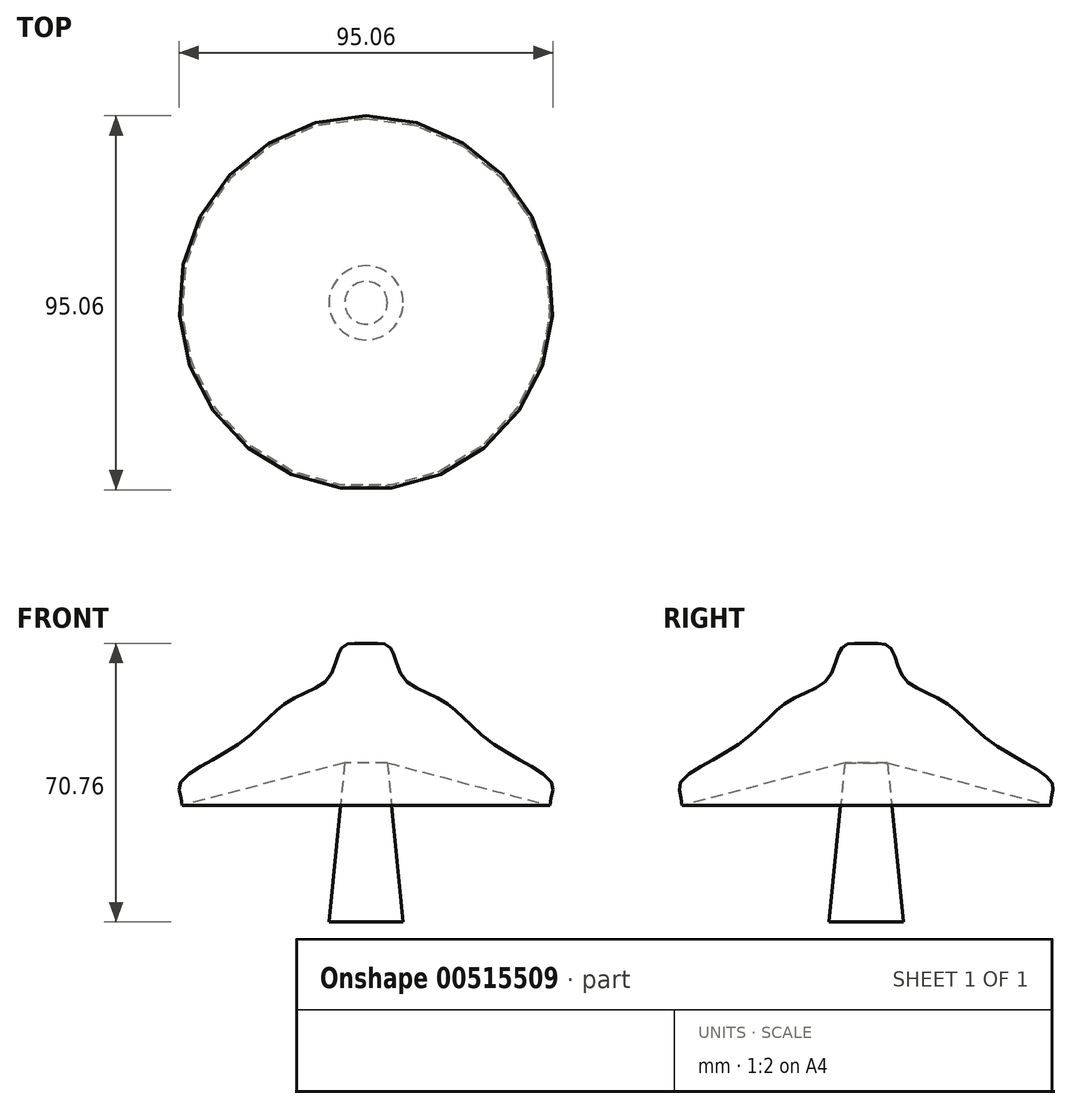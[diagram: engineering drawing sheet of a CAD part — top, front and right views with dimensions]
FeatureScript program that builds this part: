
annotation { "Feature Type Name" : "Feature", "Feature Type Description" : "" }
export const myFeature = defineFeature(function(context is Context, id is Id, definition is map)
    precondition{}
    {
        {
            var Q0;
            Q0=qCreatedBy(makeId("Right.planeOp"),FACE);
            var sketch = newSketch(context, id + "F0", { "sketchPlane" : qUnion([Q0])});
            skLineSegment(sketch, "E0.bottom", {"start": v(0, -29.54) * mm, "end": v(9.41, -29.54) * mm});
            skLineSegment(sketch, "E0.left", {"start": v(0, -29.54) * mm, "end": v(0, -29.54) * mm});
            skLineSegment(sketch, "E0.right", {"start": v(9.41, -29.54) * mm, "end": v(5.42, 10.88) * mm});
            skLineSegment(sketch, "E1", {"start": v(5.42, 10.88) * mm, "end": v(46.76, 0) * mm});
            skPoint(sketch, "E2.5.internal.orphan", {"position": v(0, 33.42) * mm});
            skPoint(sketch, "E2.6.internal.orphan", {"position": v(0, 33.42) * mm});
            skFitSpline(sketch, "E3", {"points": [v(46.76, 0) * mm, v(47.3, 5.62) * mm, v(32.27, 15.7) * mm, v(19.51, 26.59) * mm, v(9.35, 32.63) * mm, v(5.79, 40.49) * mm, v(0, 41.12) * mm], "startDerivative": vector(-0.99, 57.25) * mm, "endDerivative": vector(-43.63, 0.91) * mm});
            skLineSegment(sketch, "E4", {"start": v(0, 41.12) * mm, "end": v(0, -29.54) * mm});
            skSolve(sketch);
        }
        {
            var Q0;
            Q0 = qSketchRegion(id + "F0", true);
            var Q1;
            Q1=sQuery(id+"F0.wireOp",EDGE,"E4");
            revolve(context, id + "F1", {"entities" : qUnion([Q0]), "axis" : qUnion([Q1]), "revolveType" : RevolveType.FULL});
        }
    });
